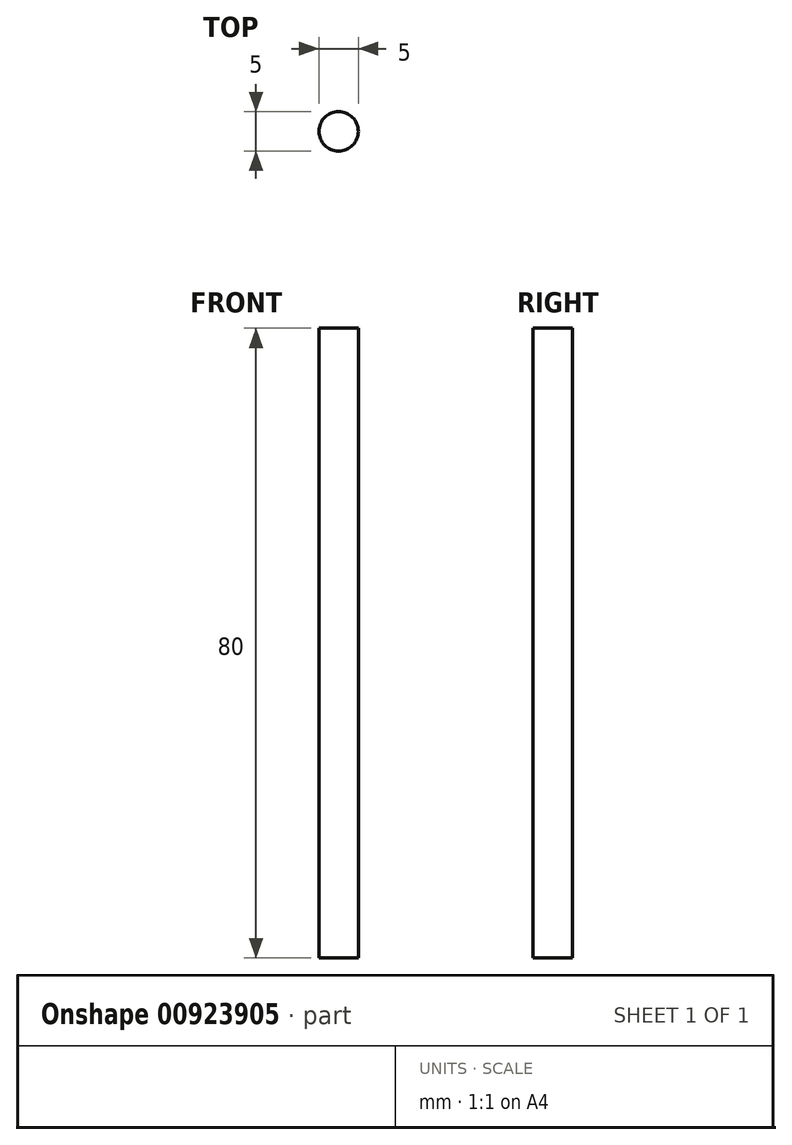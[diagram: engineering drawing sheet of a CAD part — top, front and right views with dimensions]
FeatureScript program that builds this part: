
annotation { "Feature Type Name" : "Feature", "Feature Type Description" : "" }
export const myFeature = defineFeature(function(context is Context, id is Id, definition is map)
    precondition{}
    {
        {
            var Q0;
            Q0=qCreatedBy(makeId("Top.planeOp"),FACE);
            var sketch = newSketch(context, id + "F0", { "sketchPlane" : qUnion([Q0])});
            skCircle(sketch, "E0", {"center": v(0, 0) * mm, "radius": 2.5 * mm});
            skSolve(sketch);
        }
        {
            var Q0;
            Q0=makeQuery(id+"F0.imprint","IMPRINT",FACE,{"disambiguationData":[TD([[makeQuery(id+"F0.imprint","IMPRINT",EDGE,{"derivedFrom":sQuery(id+"F0.wireOp",EDGE,"E0")}),1.0]])]});
            extrude(context, id + "F1", {"entities" : qUnion([Q0]), "depth" : 80 * mm, "offsetDistance" : 25 * mm});
        }
    });
